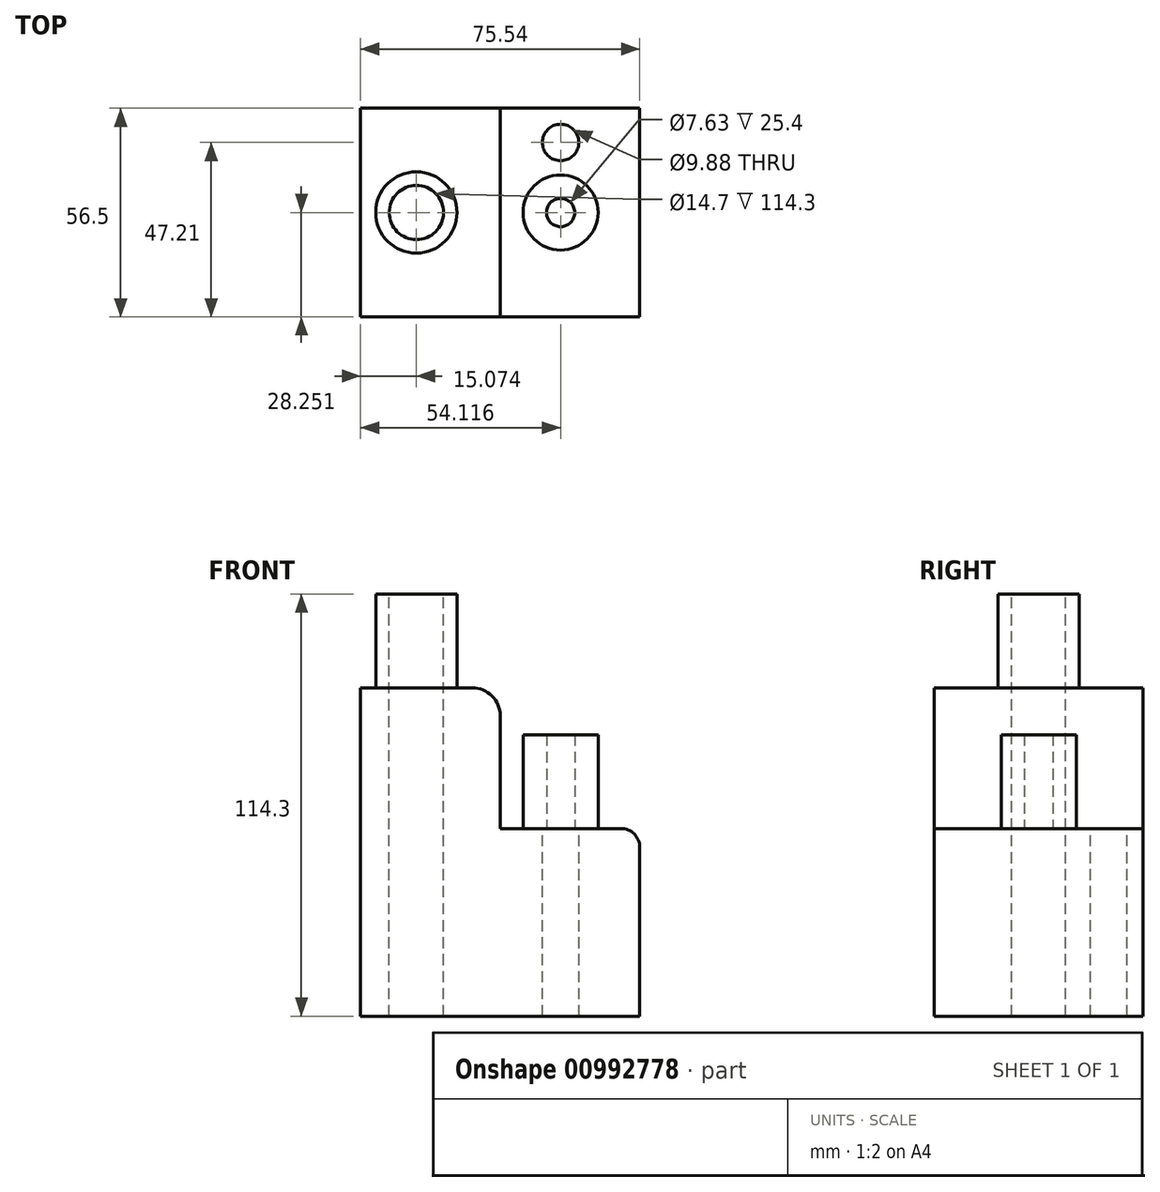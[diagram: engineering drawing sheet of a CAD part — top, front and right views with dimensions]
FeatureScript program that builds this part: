
annotation { "Feature Type Name" : "Feature", "Feature Type Description" : "" }
export const myFeature = defineFeature(function(context is Context, id is Id, definition is map)
    precondition{}
    {
        {
            var Q0;
            Q0=qCreatedBy(makeId("Top.planeOp"),FACE);
            var sketch = newSketch(context, id + "F0", { "sketchPlane" : qUnion([Q0])});
            skLineSegment(sketch, "E0.bottom", {"start": v(-28.35, 20.25) * mm, "end": v(47.2, 20.25) * mm});
            skLineSegment(sketch, "E0.top", {"start": v(-28.35, -36.25) * mm, "end": v(47.2, -36.25) * mm});
            skLineSegment(sketch, "E0.left", {"start": v(-28.35, 20.25) * mm, "end": v(-28.35, -36.25) * mm});
            skLineSegment(sketch, "E0.right", {"start": v(47.2, 20.25) * mm, "end": v(47.2, -36.25) * mm});
            skSolve(sketch);
        }
        {
            var Q0;
            Q0=makeQuery(id+"F0.imprint","IMPRINT",FACE,{"disambiguationData":[TD([[makeQuery(id+"F0.imprint","IMPRINT",EDGE,{"derivedFrom":sQuery(id+"F0.wireOp",EDGE,"E0.bottom")}),-1.0]])]});
            extrude(context, id + "F1", {"entities" : qUnion([Q0]), "depth" : 50.8 * mm, "offsetDistance" : 25.4 * mm});
        }
        {
            var Q0;
            Q0=makeQuery(id+"F1.opExtrude","CAP_FACE",FACE,{"disambiguationData":[OSD([sQuery(id+"F0.wireOp",EDGE,"E0.bottom"),sQuery(id+"F0.wireOp",EDGE,"E0.top"),sQuery(id+"F0.wireOp",EDGE,"E0.left"),sQuery(id+"F0.wireOp",EDGE,"E0.right")])],"isStart":false});
            var sketch = newSketch(context, id + "F2", { "sketchPlane" : qUnion([Q0])});
            skLineSegment(sketch, "E1", {"start": v(9.42, 20.25) * mm, "end": v(9.42, -36.25) * mm});
            skSolve(sketch);
        }
        {
            var Q0;
            {var subQ0=sQuery(id+"F2.wireOp",EDGE,"E1");Q0=makeQuery(id+"F2.imprint","IMPRINT",FACE,{"disambiguationData":[TD([[makeQuery(id+"F2.imprint","IMPRINT",EDGE,{"derivedFrom":subQ0}),-1.0]])]});}
            extrude(context, id + "F3", {"entities" : qUnion([Q0]), "operationType" : NewBodyOperationType.ADD, "depth" : 38.1 * mm, "offsetDistance" : 25.4 * mm});
        }
        {
            var Q0;
            Q0=makeQuery(id+"F3.opExtrude","CAP_EDGE",EDGE,{"disambiguationData":[OSD([sQuery(id+"F2.wireOp",EDGE,"E1")])],"isStart":false});
            fillet(context, id + "F4", {"entities" : qUnion([Q0]), "radius" : 7.62 * mm, "tangentPropagation" : true, "allowEdgeOverflow" : false});
        }
        {
            var Q0;
            Q0=makeQuery(id+"F1.opExtrude","CAP_EDGE",EDGE,{"disambiguationData":[OSD([sQuery(id+"F0.wireOp",EDGE,"E0.right")])],"isStart":false});
            fillet(context, id + "F5", {"entities" : qUnion([Q0]), "radius" : 5.08 * mm, "tangentPropagation" : true, "allowEdgeOverflow" : false});
        }
        {
            var Q0;
            Q0=makeQuery(id+"F3.opExtrude","CAP_FACE",FACE,{"disambiguationData":[OSD([sQuery(id+"F0.wireOp",EDGE,"E0.bottom"),sQuery(id+"F0.wireOp",EDGE,"E0.top"),sQuery(id+"F0.wireOp",EDGE,"E0.left"),sQuery(id+"F2.wireOp",EDGE,"E1")])],"isStart":false});
            var sketch = newSketch(context, id + "F6", { "sketchPlane" : qUnion([Q0])});
            skCircle(sketch, "E2", {"center": v(-13.28, -8) * mm, "radius": 11 * mm});
            skPoint(sketch, "E2.centerSnap0", {"position": v(-28.35, -8) * mm});
            skPoint(sketch, "E2.centerSnap1", {"position": v(-13.28, 20.25) * mm});
            skSolve(sketch);
        }
        {
            var Q0;
            Q0=makeQuery(id+"F1.opExtrude","CAP_FACE",FACE,{"disambiguationData":[OSD([sQuery(id+"F0.wireOp",EDGE,"E0.bottom"),sQuery(id+"F0.wireOp",EDGE,"E0.top"),sQuery(id+"F0.wireOp",EDGE,"E0.left"),sQuery(id+"F0.wireOp",EDGE,"E0.right")])],"isStart":false});
            var sketch = newSketch(context, id + "F7", { "sketchPlane" : qUnion([Q0])});
            skCircle(sketch, "E3", {"center": v(25.77, -8) * mm, "radius": 10.16 * mm});
            skPoint(sketch, "E3.centerSnap0", {"position": v(9.42, -8) * mm});
            skPoint(sketch, "E3.centerSnap1", {"position": v(25.77, 20.25) * mm});
            skCircle(sketch, "E4", {"center": v(25.77, -8) * mm, "radius": 3.82 * mm});
            skCircle(sketch, "E5", {"center": v(25.77, 10.96) * mm, "radius": 4.94 * mm});
            skSolve(sketch);
        }
        {
            var Q0;
            Q0=makeQuery(id+"F6.imprint","IMPRINT",FACE,{"disambiguationData":[TD([[makeQuery(id+"F6.imprint","IMPRINT",EDGE,{"derivedFrom":sQuery(id+"F6.wireOp",EDGE,"E2")}),1.0]])]});
            extrude(context, id + "F8", {"entities" : qUnion([Q0]), "operationType" : NewBodyOperationType.ADD, "depth" : 25.4 * mm, "offsetDistance" : 25.4 * mm});
        }
        {
            var Q0;
            Q0=makeQuery(id+"F7.imprint","IMPRINT",FACE,{"disambiguationData":[TD([[makeQuery(id+"F7.imprint","IMPRINT",EDGE,{"derivedFrom":sQuery(id+"F7.wireOp",EDGE,"E3")}),1.0]])]});
            extrude(context, id + "F9", {"entities" : qUnion([Q0]), "operationType" : NewBodyOperationType.ADD, "depth" : 25.4 * mm, "offsetDistance" : 25.4 * mm});
        }
        {
            var Q0;
            Q0=makeQuery(id+"F7.imprint","IMPRINT",FACE,{"disambiguationData":[TD([[makeQuery(id+"F7.imprint","IMPRINT",EDGE,{"derivedFrom":sQuery(id+"F7.wireOp",EDGE,"E5")}),1.0]])]});
            extrude(context, id + "F10", {"entities" : qUnion([Q0]), "operationType" : NewBodyOperationType.REMOVE, "oppositeDirection" : true, "depth" : 142.26 * mm, "offsetDistance" : 25.4 * mm});
        }
        {
            var Q0;
            Q0=makeQuery(id+"F8.opExtrude","CAP_FACE",FACE,{"disambiguationData":[OSD([sQuery(id+"F6.wireOp",EDGE,"E2")])],"isStart":false});
            var sketch = newSketch(context, id + "F11", { "sketchPlane" : qUnion([Q0])});
            skCircle(sketch, "E6", {"center": v(-13.28, -8) * mm, "radius": 7.35 * mm});
            skSolve(sketch);
        }
        {
            var Q0;
            Q0=makeQuery(id+"F11.imprint","IMPRINT",FACE,{"disambiguationData":[TD([[makeQuery(id+"F11.imprint","IMPRINT",EDGE,{"derivedFrom":sQuery(id+"F11.wireOp",EDGE,"E6")}),1.0]])]});
            extrude(context, id + "F12", {"entities" : qUnion([Q0]), "operationType" : NewBodyOperationType.REMOVE, "oppositeDirection" : true, "depth" : 124.53 * mm, "offsetDistance" : 25.4 * mm});
        }
    });
